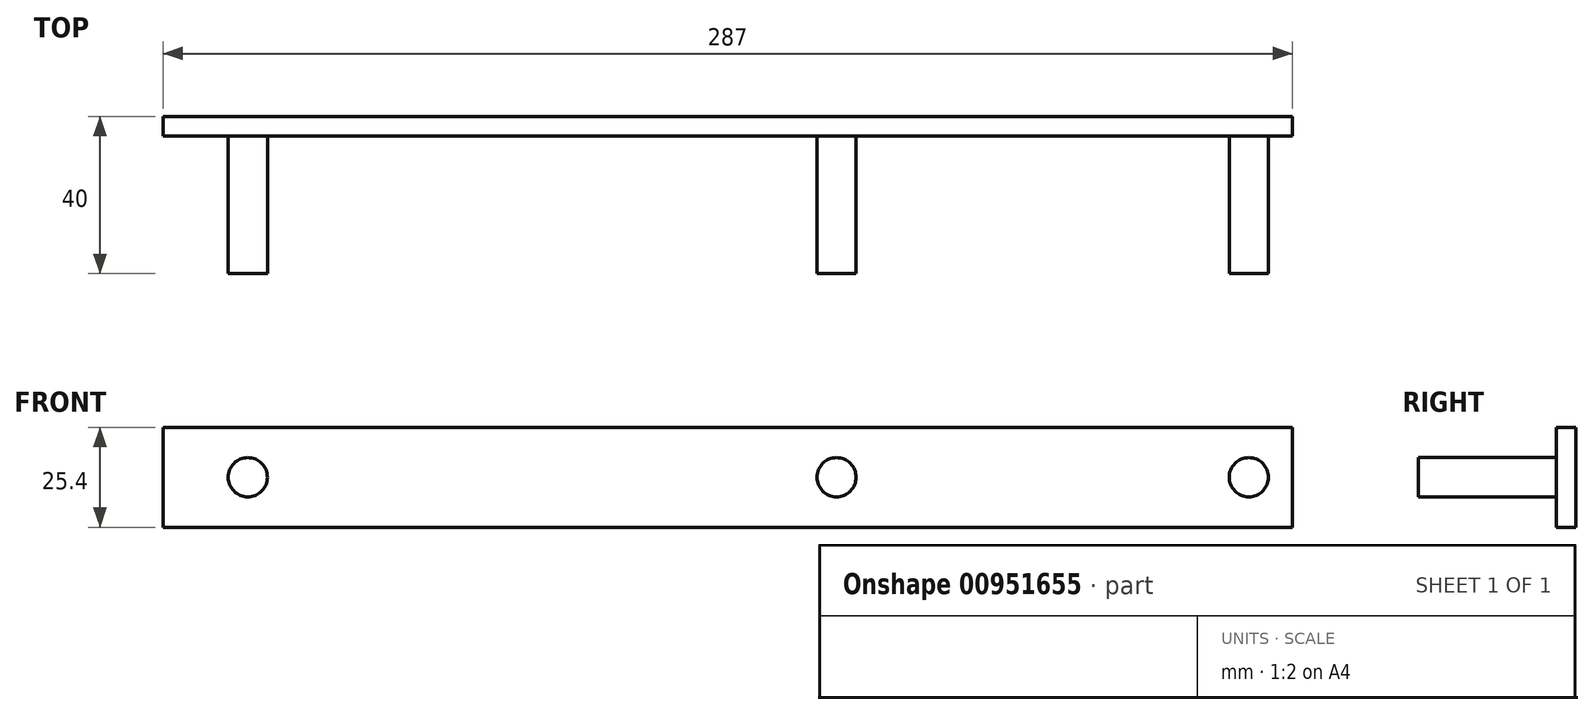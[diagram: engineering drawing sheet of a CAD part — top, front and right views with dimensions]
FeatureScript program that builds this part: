
annotation { "Feature Type Name" : "Feature", "Feature Type Description" : "" }
export const myFeature = defineFeature(function(context is Context, id is Id, definition is map)
    precondition{}
    {
        {
            var Q0;
            Q0=qCreatedBy(makeId("Front.planeOp"),FACE);
            var sketch = newSketch(context, id + "F0", { "sketchPlane" : qUnion([Q0])});
            skLineSegment(sketch, "E0.bottom", {"start": v(-63.5, -12.7) * mm, "end": v(63.5, -12.7) * mm});
            skLineSegment(sketch, "E0.top", {"start": v(-63.5, 12.7) * mm, "end": v(63.5, 12.7) * mm});
            skLineSegment(sketch, "E0.left", {"start": v(-63.5, -12.7) * mm, "end": v(-63.5, 12.7) * mm});
            skLineSegment(sketch, "E0.right", {"start": v(63.5, -12.7) * mm, "end": v(63.5, 12.7) * mm});
            skLineSegment(sketch, "E1", {"start": v(0, 0) * mm, "end": v(-63.5, 0) * mm, "construction": true});
            skLineSegment(sketch, "E2", {"start": v(0, 0) * mm, "end": v(63.5, 0) * mm, "construction": true});
            skSolve(sketch);
        }
        {
            var Q0;
            Q0=qSketchRegion(id+"F0",true);
            extrude(context, id + "F1", {"entities" : qUnion([Q0]), "oppositeDirection" : true, "depth" : 5 * mm, "offsetDistance" : 25 * mm});
        }
        {
            var Q0;
            Q0=qCreatedBy(makeId("Front.planeOp"),FACE);
            var sketch = newSketch(context, id + "F2", { "sketchPlane" : qUnion([Q0])});
            skLineSegment(sketch, "E3.bottom", {"start": v(-63.5, -12.7) * mm, "end": v(-223.5, -12.7) * mm});
            skLineSegment(sketch, "E3.top", {"start": v(-63.5, 12.7) * mm, "end": v(-223.5, 12.7) * mm});
            skLineSegment(sketch, "E3.left", {"start": v(-63.5, -12.7) * mm, "end": v(-63.5, 12.7) * mm});
            skLineSegment(sketch, "E3.right", {"start": v(-223.5, -12.7) * mm, "end": v(-223.5, 12.7) * mm});
            skSolve(sketch);
        }
        {
            var Q0;
            Q0=qSketchRegion(id+"F2",true);
            var Q1;
            Q1=makeQuery(id+"F1.opExtrude","CAP_FACE",FACE,{"disambiguationData":[OSD([sQuery(id+"F0.wireOp",EDGE,"E0.bottom"),sQuery(id+"F0.wireOp",EDGE,"E0.top"),sQuery(id+"F0.wireOp",EDGE,"E0.left"),sQuery(id+"F0.wireOp",EDGE,"E0.right")])],"isStart":false});
            extrude(context, id + "F3", {"entities" : qUnion([Q0]), "operationType" : NewBodyOperationType.ADD, "endBound" : BoundingType.UP_TO_SURFACE, "oppositeDirection" : true, "depth" : 25 * mm, "endBoundEntityFace" : qUnion([Q1]), "offsetDistance" : 25 * mm});
        }
        {
            var Q0;
            Q0=makeQuery(id+"F3.boolean.opBoolean","MERGE",FACE,{"derivedFrom":[makeQuery(id+"F1.opExtrude","CAP_FACE",FACE,{"disambiguationData":[OSD([sQuery(id+"F0.wireOp",EDGE,"E0.bottom"),sQuery(id+"F0.wireOp",EDGE,"E0.top"),sQuery(id+"F0.wireOp",EDGE,"E0.left"),sQuery(id+"F0.wireOp",EDGE,"E0.right")])],"isStart":false}),makeQuery(id+"F3.opExtrude","CAP_FACE",FACE,{"disambiguationData":[OSD([sQuery(id+"F2.wireOp",EDGE,"E3.bottom"),sQuery(id+"F2.wireOp",EDGE,"E3.top"),sQuery(id+"F2.wireOp",EDGE,"E3.left"),sQuery(id+"F2.wireOp",EDGE,"E3.right")])],"isStart":false})]});
            var sketch = newSketch(context, id + "F4", { "sketchPlane" : qUnion([Q0])});
            skCircle(sketch, "E4", {"center": v(-52.38, 0) * mm, "radius": 4.98 * mm});
            skCircle(sketch, "E5", {"center": v(52.38, 0) * mm, "radius": 4.98 * mm});
            skLineSegment(sketch, "E6", {"start": v(0, 0) * mm, "end": v(-52.38, 0) * mm, "construction": true});
            skLineSegment(sketch, "E7", {"start": v(0, 0) * mm, "end": v(52.38, 0) * mm, "construction": true});
            skCircle(sketch, "E8", {"center": v(201.93, 0) * mm, "radius": 4.98 * mm});
            skSolve(sketch);
        }
        {
            var Q0;
            Q0=qSketchRegion(id+"F4",true);
            extrude(context, id + "F5", {"entities" : qUnion([Q0]), "operationType" : NewBodyOperationType.ADD, "oppositeDirection" : true, "depth" : 40 * mm, "offsetDistance" : 25 * mm});
        }
    });
